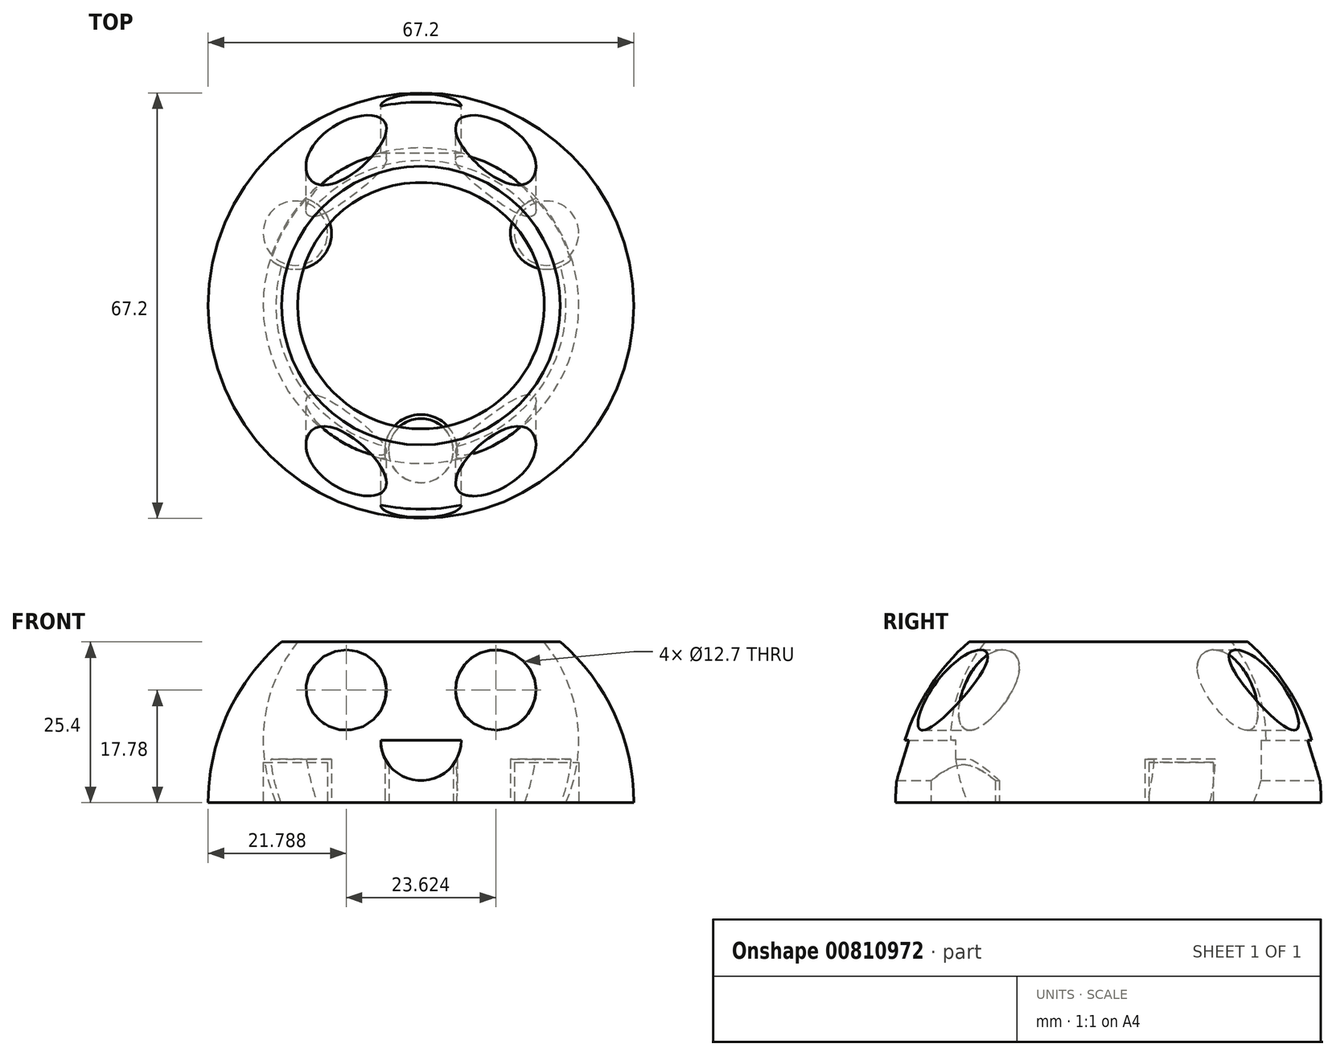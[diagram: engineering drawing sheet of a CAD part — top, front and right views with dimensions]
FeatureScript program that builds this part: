
annotation { "Feature Type Name" : "Feature", "Feature Type Description" : "" }
export const myFeature = defineFeature(function(context is Context, id is Id, definition is map)
    precondition{}
    {
        {
            var Q0;
            Q0=qCreatedBy(makeId("Front.planeOp"),FACE);
            var sketch = newSketch(context, id + "F0", { "sketchPlane" : qUnion([Q0])});
            skLineSegment(sketch, "E0", {"start": v(-33.6, 0) * mm, "end": v(33.6, 0) * mm});
            skLineSegment(sketch, "E1", {"start": v(-33.6, 0) * mm, "end": v(-22.91, 0) * mm});
            skLineSegment(sketch, "E2", {"start": v(0, 0) * mm, "end": v(0, 25.4) * mm, "construction": true});
            skLineSegment(sketch, "E3", {"start": v(-19.46, 25.4) * mm, "end": v(-22, 25.4) * mm});
            skArc(sketch, "E4", {"start": v(-33.6, 0) * mm, "mid": v(-30.57, 13.96) * mm, "end": v(-22, 25.4) * mm});
            skArc(sketch, "E5", {"start": v(-19.46, 25.4) * mm, "mid": v(-24.7, 13.18) * mm, "end": v(-22.91, 0) * mm});
            skArc(sketch, "E6.MirrorCS", {"start": v(19.46, 25.4) * mm, "mid": v(24.7, 13.18) * mm, "end": v(22.91, 0) * mm});
            skArc(sketch, "E7.MirrorCS", {"start": v(33.6, 0) * mm, "mid": v(30.57, 13.96) * mm, "end": v(22, 25.4) * mm});
            skLineSegment(sketch, "E8.MirrorCS", {"start": v(19.46, 25.4) * mm, "end": v(22, 25.4) * mm});
            skSolve(sketch);
        }
        {
            var Q0;
            Q0 = qSketchRegion(id + "F0", true);
            var Q1;
            Q1=sQuery(id+"F0.wireOp",EDGE,"E2");
            revolve(context, id + "F1", {"surfaceOperationType" : NewSurfaceOperationType.NEW, "entities" : qUnion([Q0]), "axis" : qUnion([Q1]), "revolveType" : RevolveType.FULL});
        }
        {
            var Q0;
            Q0=makeQuery(id+"F1.opRevolve","SWEPT_BODY",BODY,{"disambiguationData":[OSD([sQuery(id+"F0.wireOp",EDGE,"E1"),sQuery(id+"F0.wireOp",EDGE,"E3"),sQuery(id+"F0.wireOp",EDGE,"E4"),sQuery(id+"F0.wireOp",EDGE,"E5")])]});
            deleteBodies(context, id + "F2", {"entities" : qUnion([Q0])});
        }
        {
            var Q0;
            Q0=makeQuery(id+"F1.opRevolve","SWEPT_FACE",FACE,{"disambiguationData":[OSD([sQuery(id+"F0.wireOp",EDGE,"E0")])]});
            var sketch = newSketch(context, id + "F3", { "sketchPlane" : qUnion([Q0])});
            skCircle(sketch, "E9", {"center": v(0, 22.91) * mm, "radius": 5.72 * mm});
            skCircle(sketch, "E10", {"center": v(0, 22.91) * mm, "radius": 5.08 * mm});
            skCircle(sketch, "E11.1.0", {"center": v(-19.84, -11.46) * mm, "radius": 5.08 * mm});
            skCircle(sketch, "E11.1.1", {"center": v(-19.84, -11.46) * mm, "radius": 5.72 * mm});
            skCircle(sketch, "E11.2.0", {"center": v(19.84, -11.46) * mm, "radius": 5.08 * mm});
            skCircle(sketch, "E11.2.1", {"center": v(19.84, -11.46) * mm, "radius": 5.72 * mm});
            skPoint(sketch, "E11.center", {"position": v(0, 0) * mm});
            skSolve(sketch);
        }
        {
            var Q0;
            Q0 = qSketchRegion(id + "F3", true);
            var Q1;
            {var subQ0=sQuery(id+"F3.wireOp",EDGE,"E11.1.0");var subQ1=makeQuery(id+"F1.opRevolve","SWEPT_EDGE",EDGE,{"disambiguationData":[OSD([sQuery(id+"F0.wireOp",EDGE,"E0"),sQuery(id+"F0.wireOp",EDGE,"E6.MirrorCS")])]});var subQ2=makeQuery(id+"F3.imprint","INTERSECT",VERTEX,{"disambiguationData":[OD(0.0)],"derivedFrom":[subQ1,subQ0]});Q1=makeQuery(id+"F3.imprint","IMPRINT",FACE,{"disambiguationData":[TD([[makeQuery(id+"F3.imprint","IMPRINT",EDGE,{"disambiguationData":[TD([[subQ2,-1.0]])],"derivedFrom":subQ0}),1.0]])]});}
            var Q2;
            {var subQ0=sQuery(id+"F3.wireOp",EDGE,"E11.1.0");var subQ1=makeQuery(id+"F1.opRevolve","SWEPT_EDGE",EDGE,{"disambiguationData":[OSD([sQuery(id+"F0.wireOp",EDGE,"E0"),sQuery(id+"F0.wireOp",EDGE,"E6.MirrorCS")])]});var subQ2=makeQuery(id+"F3.imprint","INTERSECT",VERTEX,{"disambiguationData":[OD(0.0)],"derivedFrom":[subQ1,subQ0]});Q2=makeQuery(id+"F3.imprint","IMPRINT",FACE,{"disambiguationData":[TD([[makeQuery(id+"F3.imprint","IMPRINT",EDGE,{"disambiguationData":[TD([[subQ2,1.0]])],"derivedFrom":subQ0}),1.0]])]});}
            var Q3;
            {var subQ0=sQuery(id+"F3.wireOp",EDGE,"E11.2.0");var subQ1=makeQuery(id+"F1.opRevolve","SWEPT_EDGE",EDGE,{"disambiguationData":[OSD([sQuery(id+"F0.wireOp",EDGE,"E0"),sQuery(id+"F0.wireOp",EDGE,"E6.MirrorCS")])]});var subQ2=makeQuery(id+"F3.imprint","INTERSECT",VERTEX,{"disambiguationData":[OD(0.0)],"derivedFrom":[subQ1,subQ0]});Q3=makeQuery(id+"F3.imprint","IMPRINT",FACE,{"disambiguationData":[TD([[makeQuery(id+"F3.imprint","IMPRINT",EDGE,{"disambiguationData":[TD([[subQ2,1.0]])],"derivedFrom":subQ0}),1.0]])]});}
            var Q4;
            {var subQ0=sQuery(id+"F3.wireOp",EDGE,"E11.2.0");var subQ1=makeQuery(id+"F1.opRevolve","SWEPT_EDGE",EDGE,{"disambiguationData":[OSD([sQuery(id+"F0.wireOp",EDGE,"E0"),sQuery(id+"F0.wireOp",EDGE,"E6.MirrorCS")])]});var subQ2=makeQuery(id+"F3.imprint","INTERSECT",VERTEX,{"disambiguationData":[OD(0.0)],"derivedFrom":[subQ1,subQ0]});Q4=makeQuery(id+"F3.imprint","IMPRINT",FACE,{"disambiguationData":[TD([[makeQuery(id+"F3.imprint","IMPRINT",EDGE,{"disambiguationData":[TD([[subQ2,-1.0]])],"derivedFrom":subQ0}),1.0]])]});}
            var Q5;
            {var subQ0=sQuery(id+"F3.wireOp",EDGE,"E10");var subQ1=makeQuery(id+"F1.opRevolve","SWEPT_EDGE",EDGE,{"disambiguationData":[OSD([sQuery(id+"F0.wireOp",EDGE,"E0"),sQuery(id+"F0.wireOp",EDGE,"E6.MirrorCS")])]});var subQ2=makeQuery(id+"F3.imprint","INTERSECT",VERTEX,{"disambiguationData":[OD(0.0)],"derivedFrom":[subQ1,subQ0]});Q5=makeQuery(id+"F3.imprint","IMPRINT",FACE,{"disambiguationData":[TD([[makeQuery(id+"F3.imprint","IMPRINT",EDGE,{"disambiguationData":[TD([[subQ2,1.0]])],"derivedFrom":subQ0}),1.0]])]});}
            var Q6;
            {var subQ0=sQuery(id+"F3.wireOp",EDGE,"E10");var subQ1=makeQuery(id+"F1.opRevolve","SWEPT_EDGE",EDGE,{"disambiguationData":[OSD([sQuery(id+"F0.wireOp",EDGE,"E0"),sQuery(id+"F0.wireOp",EDGE,"E6.MirrorCS")])]});var subQ2=makeQuery(id+"F3.imprint","INTERSECT",VERTEX,{"disambiguationData":[OD(0.0)],"derivedFrom":[subQ1,subQ0]});Q6=makeQuery(id+"F3.imprint","IMPRINT",FACE,{"disambiguationData":[TD([[makeQuery(id+"F3.imprint","IMPRINT",EDGE,{"disambiguationData":[TD([[subQ2,-1.0]])],"derivedFrom":subQ0}),1.0]])]});}
            extrude(context, id + "F4", {"entities" : qUnion([Q0, Q1, Q2, Q3, Q4, Q5, Q6]), "operationType" : NewBodyOperationType.ADD, "oppositeDirection" : true, "depth" : 6.86 * mm, "offsetDistance" : 25.4 * mm});
        }
        {
            var Q0;
            {var subQ0=sQuery(id+"F3.wireOp",EDGE,"E11.1.0");var subQ1=makeQuery(id+"F1.opRevolve","SWEPT_EDGE",EDGE,{"disambiguationData":[OSD([sQuery(id+"F0.wireOp",EDGE,"E0"),sQuery(id+"F0.wireOp",EDGE,"E6.MirrorCS")])]});var subQ2=makeQuery(id+"F3.imprint","INTERSECT",VERTEX,{"disambiguationData":[OD(0.0)],"derivedFrom":[subQ1,subQ0]});Q0=makeQuery(id+"F3.imprint","IMPRINT",FACE,{"disambiguationData":[TD([[makeQuery(id+"F3.imprint","IMPRINT",EDGE,{"disambiguationData":[TD([[subQ2,1.0]])],"derivedFrom":subQ0}),1.0]])]});}
            var Q1;
            {var subQ0=sQuery(id+"F3.wireOp",EDGE,"E11.1.0");var subQ1=makeQuery(id+"F1.opRevolve","SWEPT_EDGE",EDGE,{"disambiguationData":[OSD([sQuery(id+"F0.wireOp",EDGE,"E0"),sQuery(id+"F0.wireOp",EDGE,"E6.MirrorCS")])]});var subQ2=makeQuery(id+"F3.imprint","INTERSECT",VERTEX,{"disambiguationData":[OD(0.0)],"derivedFrom":[subQ1,subQ0]});Q1=makeQuery(id+"F3.imprint","IMPRINT",FACE,{"disambiguationData":[TD([[makeQuery(id+"F3.imprint","IMPRINT",EDGE,{"disambiguationData":[TD([[subQ2,-1.0]])],"derivedFrom":subQ0}),1.0]])]});}
            var Q2;
            {var subQ0=sQuery(id+"F3.wireOp",EDGE,"E10");var subQ1=makeQuery(id+"F1.opRevolve","SWEPT_EDGE",EDGE,{"disambiguationData":[OSD([sQuery(id+"F0.wireOp",EDGE,"E0"),sQuery(id+"F0.wireOp",EDGE,"E6.MirrorCS")])]});var subQ2=makeQuery(id+"F3.imprint","INTERSECT",VERTEX,{"disambiguationData":[OD(0.0)],"derivedFrom":[subQ1,subQ0]});Q2=makeQuery(id+"F3.imprint","IMPRINT",FACE,{"disambiguationData":[TD([[makeQuery(id+"F3.imprint","IMPRINT",EDGE,{"disambiguationData":[TD([[subQ2,1.0]])],"derivedFrom":subQ0}),1.0]])]});}
            var Q3;
            {var subQ0=sQuery(id+"F3.wireOp",EDGE,"E10");var subQ1=makeQuery(id+"F1.opRevolve","SWEPT_EDGE",EDGE,{"disambiguationData":[OSD([sQuery(id+"F0.wireOp",EDGE,"E0"),sQuery(id+"F0.wireOp",EDGE,"E6.MirrorCS")])]});var subQ2=makeQuery(id+"F3.imprint","INTERSECT",VERTEX,{"disambiguationData":[OD(0.0)],"derivedFrom":[subQ1,subQ0]});Q3=makeQuery(id+"F3.imprint","IMPRINT",FACE,{"disambiguationData":[TD([[makeQuery(id+"F3.imprint","IMPRINT",EDGE,{"disambiguationData":[TD([[subQ2,-1.0]])],"derivedFrom":subQ0}),1.0]])]});}
            var Q4;
            {var subQ0=sQuery(id+"F3.wireOp",EDGE,"E11.2.0");var subQ1=makeQuery(id+"F1.opRevolve","SWEPT_EDGE",EDGE,{"disambiguationData":[OSD([sQuery(id+"F0.wireOp",EDGE,"E0"),sQuery(id+"F0.wireOp",EDGE,"E6.MirrorCS")])]});var subQ2=makeQuery(id+"F3.imprint","INTERSECT",VERTEX,{"disambiguationData":[OD(0.0)],"derivedFrom":[subQ1,subQ0]});Q4=makeQuery(id+"F3.imprint","IMPRINT",FACE,{"disambiguationData":[TD([[makeQuery(id+"F3.imprint","IMPRINT",EDGE,{"disambiguationData":[TD([[subQ2,1.0]])],"derivedFrom":subQ0}),1.0]])]});}
            var Q5;
            {var subQ0=sQuery(id+"F3.wireOp",EDGE,"E11.2.0");var subQ1=makeQuery(id+"F1.opRevolve","SWEPT_EDGE",EDGE,{"disambiguationData":[OSD([sQuery(id+"F0.wireOp",EDGE,"E0"),sQuery(id+"F0.wireOp",EDGE,"E6.MirrorCS")])]});var subQ2=makeQuery(id+"F3.imprint","INTERSECT",VERTEX,{"disambiguationData":[OD(0.0)],"derivedFrom":[subQ1,subQ0]});Q5=makeQuery(id+"F3.imprint","IMPRINT",FACE,{"disambiguationData":[TD([[makeQuery(id+"F3.imprint","IMPRINT",EDGE,{"disambiguationData":[TD([[subQ2,-1.0]])],"derivedFrom":subQ0}),1.0]])]});}
            extrude(context, id + "F5", {"entities" : qUnion([Q0, Q1, Q2, Q3, Q4, Q5]), "operationType" : NewBodyOperationType.REMOVE, "oppositeDirection" : true, "depth" : 6.35 * mm, "offsetDistance" : 25.4 * mm});
        }
        {
            var Q0;
            Q0=qCreatedBy(makeId("Front.planeOp"),FACE);
            var sketch = newSketch(context, id + "F6", { "sketchPlane" : qUnion([Q0])});
            skLineSegment(sketch, "E12", {"start": v(0, 25.4) * mm, "end": v(0, 0) * mm});
            skLineSegment(sketch, "E13", {"start": v(0, 12.7) * mm, "end": v(0, 22.86) * mm});
            skLineSegment(sketch, "E14", {"start": v(0, 12.7) * mm, "end": v(0, 2.54) * mm});
            skArc(sketch, "E15.0", {"start": v(-19.46, 25.4) * mm, "mid": v(-24.7, 13.18) * mm, "end": v(-22.91, 0) * mm});
            skLineSegment(sketch, "E16", {"start": v(0, 17.78) * mm, "end": v(-23.62, 17.78) * mm});
            skCircle(sketch, "E17", {"center": v(-11.81, 17.78) * mm, "radius": 6.35 * mm});
            skCircle(sketch, "E18.MirrorC", {"center": v(11.81, 17.78) * mm, "radius": 6.35 * mm});
            skPoint(sketch, "E19.startSnap0", {"position": v(0, 7.62) * mm});
            skLineSegment(sketch, "E20", {"start": v(-6.35, 9.82) * mm, "end": v(6.35, 9.82) * mm});
            skArc(sketch, "E21", {"start": v(-6.35, 9.82) * mm, "mid": v(0, 3.47) * mm, "end": v(6.35, 9.82) * mm});
            skSolve(sketch);
        }
        {
            var Q0;
            Q0 = qSketchRegion(id + "F6", true);
            var Q1;
            Q1=makeQuery(id+"F1.opRevolve","SWEPT_FACE",FACE,{"disambiguationData":[OSD([sQuery(id+"F0.wireOp",EDGE,"E7.MirrorCS")])]});
            var Q2;
            Q2=makeQuery(id+"F1.opRevolve","SWEPT_FACE",FACE,{"disambiguationData":[OSD([sQuery(id+"F0.wireOp",EDGE,"E7.MirrorCS")])]});
            extrude(context, id + "F7", {"entities" : qUnion([Q0]), "operationType" : NewBodyOperationType.REMOVE, "endBound" : BoundingType.UP_TO_SURFACE, "depth" : 25.4 * mm, "endBoundEntityFace" : qUnion([Q1]), "offsetDistance" : 25.4 * mm, "hasSecondDirection" : true, "secondDirectionBound" : SecondDirectionBoundingType.UP_TO_SURFACE, "secondDirectionOppositeDirection" : true, "secondDirectionDepth" : 25.4 * mm, "secondDirectionBoundEntityFace" : qUnion([Q2])});
        }
    });
